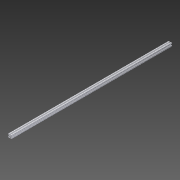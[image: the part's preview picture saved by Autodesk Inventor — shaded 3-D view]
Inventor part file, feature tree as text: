
AUTODESK INVENTOR PART (.ipt)
format: ipt  version: 2013 (Build 170138000, 138)  size: 295,424 bytes
history: native  units: in
note: dims shown in document units (in); Inventor stores cm internally (conversion verified against a paired STEP export)
features: extrude x2, imported_body x1, sketch x1
ambient origin geometry x8: Origin, YZ Plane, XZ Plane, XY Plane, X Axis, Y Axis, Z Axis, Center Point
feature tree (4):
  extrude  "Extrude1"  [1 undecoded]
  extrude  "Extrusion1"  [1 undecoded]
  imported_body  "Base1"
  sketch  "Sketch1"  dims[d0=36.0in d1=0.0in]
note: 2 required parameter values undecoded (feature->parameter linkage not recoverable at this tier; creation-order binding heuristic only, values carry confidence <= 0.55)
